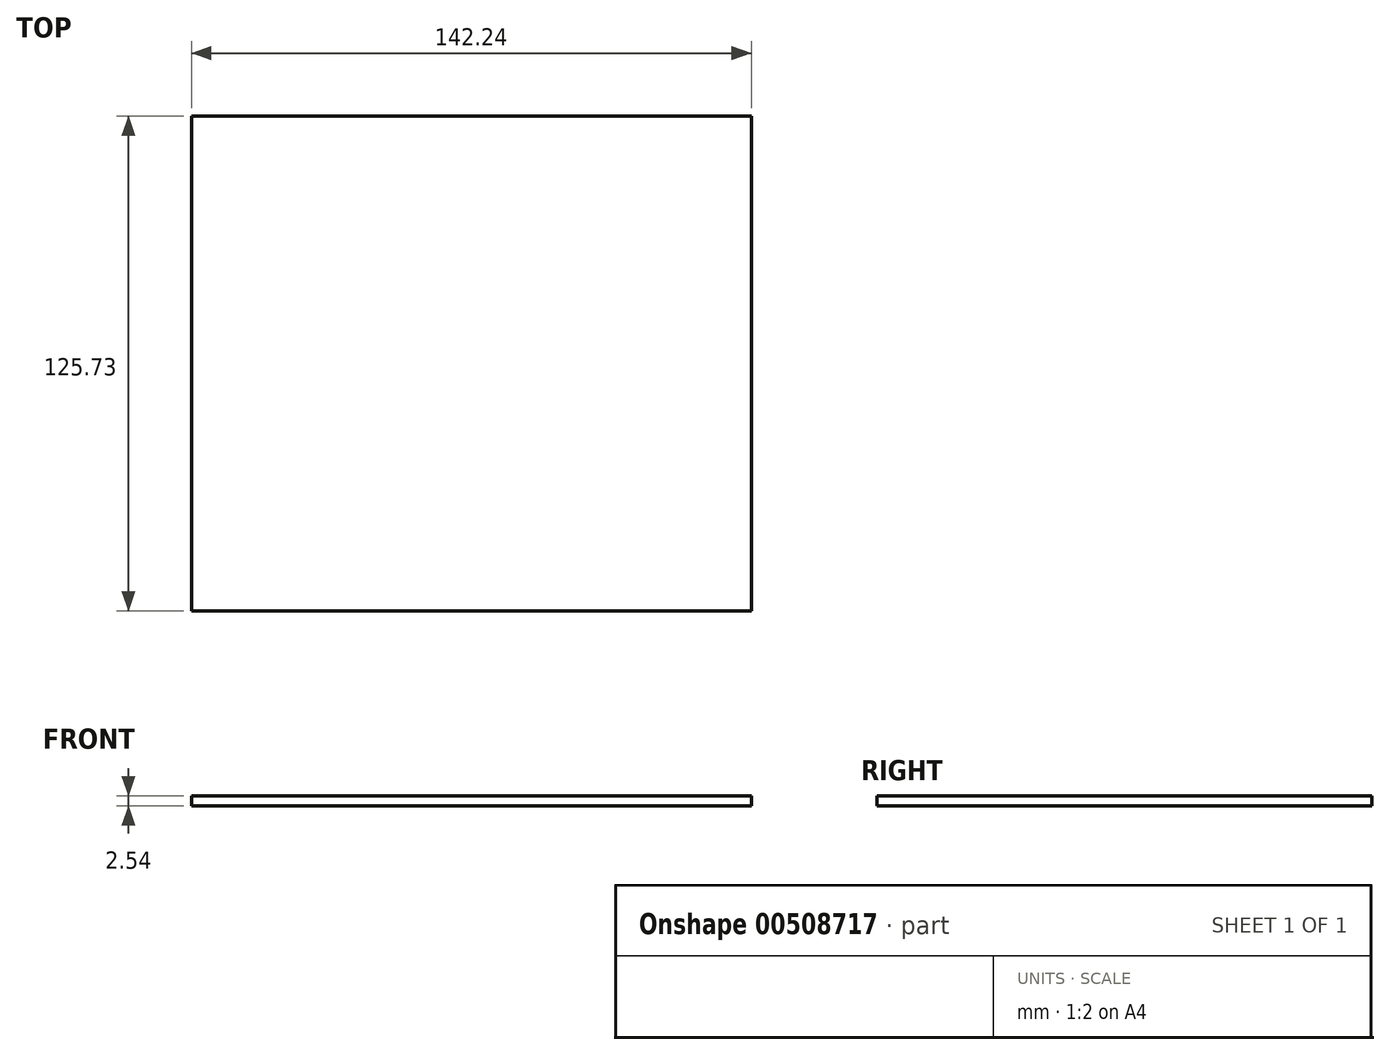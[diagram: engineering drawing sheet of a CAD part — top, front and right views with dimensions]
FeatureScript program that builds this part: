
annotation { "Feature Type Name" : "Feature", "Feature Type Description" : "" }
export const myFeature = defineFeature(function(context is Context, id is Id, definition is map)
    precondition{}
    {
        {
            var Q0;
            Q0=qCreatedBy(makeId("Front.planeOp"),FACE);
            var sketch = newSketch(context, id + "F0", { "sketchPlane" : qUnion([Q0])});
            skLineSegment(sketch, "E0", {"start": v(-92.29, 2.54) * mm, "end": v(49.95, 2.54) * mm});
            skLineSegment(sketch, "E1", {"start": v(49.95, 2.54) * mm, "end": v(49.95, 0) * mm});
            skLineSegment(sketch, "E2", {"start": v(49.95, 0) * mm, "end": v(-92.29, 0) * mm});
            skLineSegment(sketch, "E3", {"start": v(-92.29, 0) * mm, "end": v(-92.29, 2.54) * mm});
            skSolve(sketch);
        }
        {
            var Q0;
            Q0=makeQuery(id+"F0.imprint","IMPRINT",FACE,{"disambiguationData":[TD([[makeQuery(id+"F0.imprint","IMPRINT",EDGE,{"derivedFrom":sQuery(id+"F0.wireOp",EDGE,"E0")}),-1.0]])]});
            extrude(context, id + "F1", {"entities" : qUnion([Q0]), "depth" : 125.73 * mm});
        }
    });
